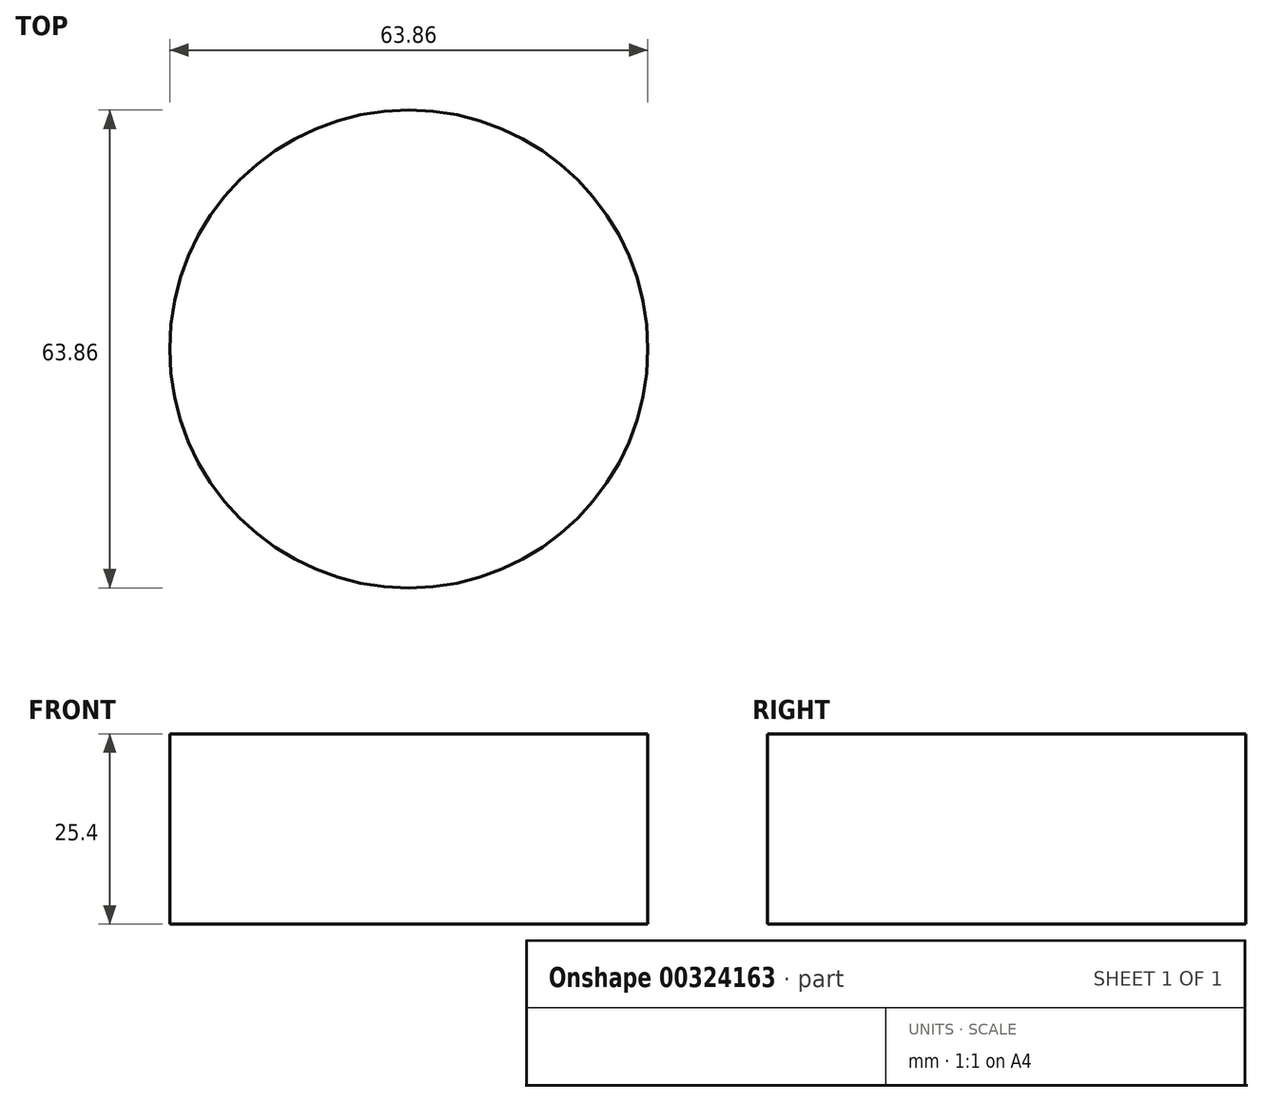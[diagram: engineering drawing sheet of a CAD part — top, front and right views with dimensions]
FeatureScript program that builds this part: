
annotation { "Feature Type Name" : "Feature", "Feature Type Description" : "" }
export const myFeature = defineFeature(function(context is Context, id is Id, definition is map)
    precondition{}
    {
        {
            var Q0;
            Q0=qCreatedBy(makeId("Top.planeOp"),FACE);
            var sketch = newSketch(context, id + "F0", { "sketchPlane" : qUnion([Q0])});
            skCircle(sketch, "E0", {"center": v(0, 0) * mm, "radius": 31.93 * mm});
            skCircle(sketch, "E1", {"center": v(0, 0) * mm, "radius": 12.66 * mm});
            skSolve(sketch);
        }
        {
            var Q0;
            Q0=makeQuery(id+"F0.imprint","IMPRINT",FACE,{"disambiguationData":[TD([[makeQuery(id+"F0.imprint","IMPRINT",EDGE,{"derivedFrom":sQuery(id+"F0.wireOp",EDGE,"E0")}),1.0]])]});
            var Q1;
            Q1=makeQuery(id+"F0.imprint","IMPRINT",FACE,{"disambiguationData":[TD([[makeQuery(id+"F0.imprint","IMPRINT",EDGE,{"derivedFrom":sQuery(id+"F0.wireOp",EDGE,"E1")}),1.0]])]});
            extrude(context, id + "F1", {"entities" : qUnion([Q0, Q1]), "oppositeDirection" : true, "depth" : 25.4 * mm});
        }
    });
